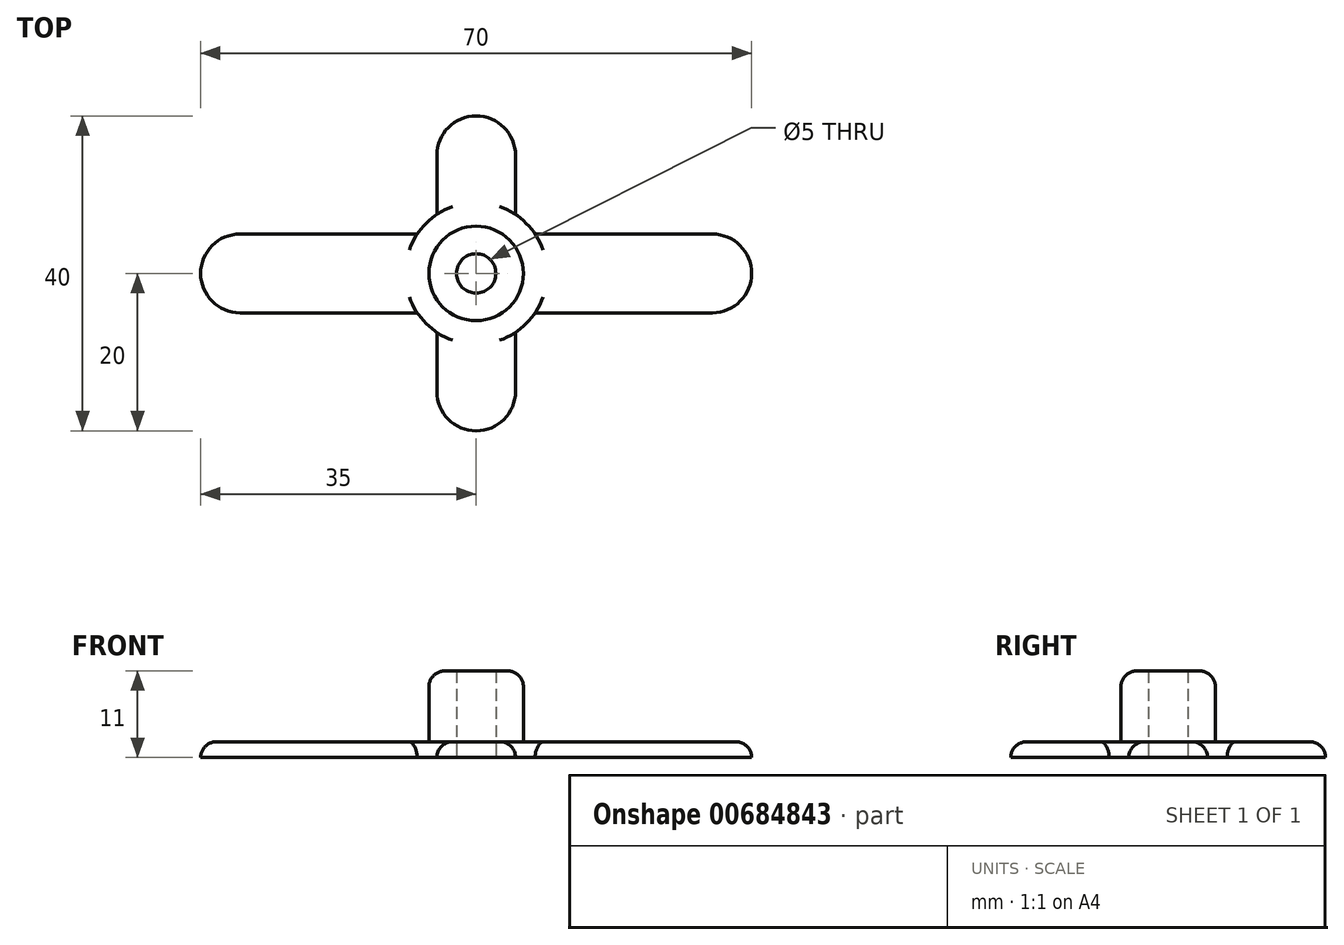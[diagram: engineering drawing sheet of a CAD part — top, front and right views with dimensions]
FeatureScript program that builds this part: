
annotation { "Feature Type Name" : "Feature", "Feature Type Description" : "" }
export const myFeature = defineFeature(function(context is Context, id is Id, definition is map)
    precondition{}
    {
        {
            var Q0;
            Q0=qCreatedBy(makeId("Top.planeOp"),FACE);
            var sketch = newSketch(context, id + "F0", { "sketchPlane" : qUnion([Q0])});
            skArc(sketch, "E0", {"start": v(-7.48, -5) * mm, "mid": v(-6.36, -6.36) * mm, "end": v(-5, -7.48) * mm});
            skCircle(sketch, "E1", {"center": v(0, 0) * mm, "radius": 2.5 * mm});
            skLineSegment(sketch, "E2", {"start": v(0, 2.5) * mm, "end": v(0, 5) * mm, "construction": true});
            skLineSegment(sketch, "E3", {"start": v(-7.48, 5) * mm, "end": v(-30, 5) * mm});
            skLineSegment(sketch, "E4", {"start": v(-30, -5) * mm, "end": v(-7.48, -5) * mm});
            skLineSegment(sketch, "E5", {"start": v(30, 5) * mm, "end": v(7.48, 5) * mm});
            skArc(sketch, "E6", {"start": v(-30, 5) * mm, "mid": v(-35, 0) * mm, "end": v(-30, -5) * mm});
            skArc(sketch, "E7", {"start": v(30, -5) * mm, "mid": v(35, 0) * mm, "end": v(30, 5) * mm});
            skLineSegment(sketch, "E8", {"start": v(-5, 7.48) * mm, "end": v(-5, 15) * mm});
            skLineSegment(sketch, "E9", {"start": v(5, 15) * mm, "end": v(5, 7.48) * mm});
            skLineSegment(sketch, "E10", {"start": v(-5, -15) * mm, "end": v(-5, -7.48) * mm});
            skLineSegment(sketch, "E11.trimOffspring", {"start": v(5, -7.48) * mm, "end": v(5, -15) * mm});
            skArc(sketch, "E12", {"start": v(5, 15) * mm, "mid": v(0, 20) * mm, "end": v(-5, 15) * mm});
            skArc(sketch, "E13", {"start": v(-5, -15) * mm, "mid": v(0, -20) * mm, "end": v(5, -15) * mm});
            skLineSegment(sketch, "E14.trimOffspring", {"start": v(7.48, -5) * mm, "end": v(30, -5) * mm});
            skArc(sketch, "E15.trimOffspring", {"start": v(-5, 7.48) * mm, "mid": v(-6.36, 6.36) * mm, "end": v(-7.48, 5) * mm});
            skArc(sketch, "E16.trimOffspring", {"start": v(7.48, 5) * mm, "mid": v(6.36, 6.36) * mm, "end": v(5, 7.48) * mm});
            skArc(sketch, "E17.trimOffspring", {"start": v(5, -7.48) * mm, "mid": v(6.36, -6.36) * mm, "end": v(7.48, -5) * mm});
            skSolve(sketch);
        }
        {
            var Q0;
            Q0=makeQuery(id+"F0.imprint","IMPRINT",FACE,{"disambiguationData":[TD([[makeQuery(id+"F0.imprint","IMPRINT",EDGE,{"derivedFrom":sQuery(id+"F0.wireOp",EDGE,"E1")}),-1.0]])]});
            extrude(context, id + "F1", {"entities" : qUnion([Q0]), "depth" : 2 * mm, "offsetDistance" : 25 * mm});
        }
        {
            var Q0;
            Q0=makeQuery(id+"F1.opExtrude","CAP_FACE",FACE,{"disambiguationData":[OSD([sQuery(id+"F0.wireOp",EDGE,"E0"),sQuery(id+"F0.wireOp",EDGE,"E1"),sQuery(id+"F0.wireOp",EDGE,"E3"),sQuery(id+"F0.wireOp",EDGE,"E4"),sQuery(id+"F0.wireOp",EDGE,"E5"),sQuery(id+"F0.wireOp",EDGE,"E6"),sQuery(id+"F0.wireOp",EDGE,"E7"),sQuery(id+"F0.wireOp",EDGE,"E8"),sQuery(id+"F0.wireOp",EDGE,"E9"),sQuery(id+"F0.wireOp",EDGE,"E10"),sQuery(id+"F0.wireOp",EDGE,"E11.trimOffspring"),sQuery(id+"F0.wireOp",EDGE,"E12"),sQuery(id+"F0.wireOp",EDGE,"E13"),sQuery(id+"F0.wireOp",EDGE,"E14.trimOffspring"),sQuery(id+"F0.wireOp",EDGE,"E15.trimOffspring"),sQuery(id+"F0.wireOp",EDGE,"E16.trimOffspring"),sQuery(id+"F0.wireOp",EDGE,"E17.trimOffspring")])],"isStart":false});
            var sketch = newSketch(context, id + "F2", { "sketchPlane" : qUnion([Q0])});
            skCircle(sketch, "E18", {"center": v(0, 0) * mm, "radius": 6 * mm});
            skCircle(sketch, "E19", {"center": v(0, 0) * mm, "radius": 2.5 * mm});
            skSolve(sketch);
        }
        {
            var Q0;
            Q0=makeQuery(id+"F2.imprint","IMPRINT",FACE,{"disambiguationData":[TD([[makeQuery(id+"F2.imprint","IMPRINT",EDGE,{"derivedFrom":sQuery(id+"F2.wireOp",EDGE,"E19")}),-1.0]])]});
            extrude(context, id + "F3", {"entities" : qUnion([Q0]), "operationType" : NewBodyOperationType.ADD, "depth" : 9 * mm, "offsetDistance" : 25 * mm});
        }
        {
            var Q0;
            Q0=makeQuery(id+"F3.opExtrude","CAP_EDGE",EDGE,{"disambiguationData":[OSD([sQuery(id+"F2.wireOp",EDGE,"E18")])],"isStart":false});
            fillet(context, id + "F4", {"entities" : qUnion([Q0]), "radius" : 2 * mm, "tangentPropagation" : true, "allowEdgeOverflow" : false});
        }
        {
            var Q0;
            Q0=makeQuery(id+"F1.opExtrude","CAP_EDGE",EDGE,{"disambiguationData":[OSD([sQuery(id+"F0.wireOp",EDGE,"E7")])],"isStart":false});
            var Q1;
            Q1=makeQuery(id+"F1.opExtrude","CAP_EDGE",EDGE,{"disambiguationData":[OSD([sQuery(id+"F0.wireOp",EDGE,"E12")])],"isStart":false});
            var Q2;
            Q2=makeQuery(id+"F1.opExtrude","CAP_EDGE",EDGE,{"disambiguationData":[OSD([sQuery(id+"F0.wireOp",EDGE,"E13")])],"isStart":false});
            var Q3;
            Q3=makeQuery(id+"F1.opExtrude","CAP_EDGE",EDGE,{"disambiguationData":[OSD([sQuery(id+"F0.wireOp",EDGE,"E6")])],"isStart":false});
            fillet(context, id + "F5", {"entities" : qUnion([Q0, Q1, Q2, Q3]), "radius" : 2 * mm, "tangentPropagation" : true, "allowEdgeOverflow" : false});
        }
    });
